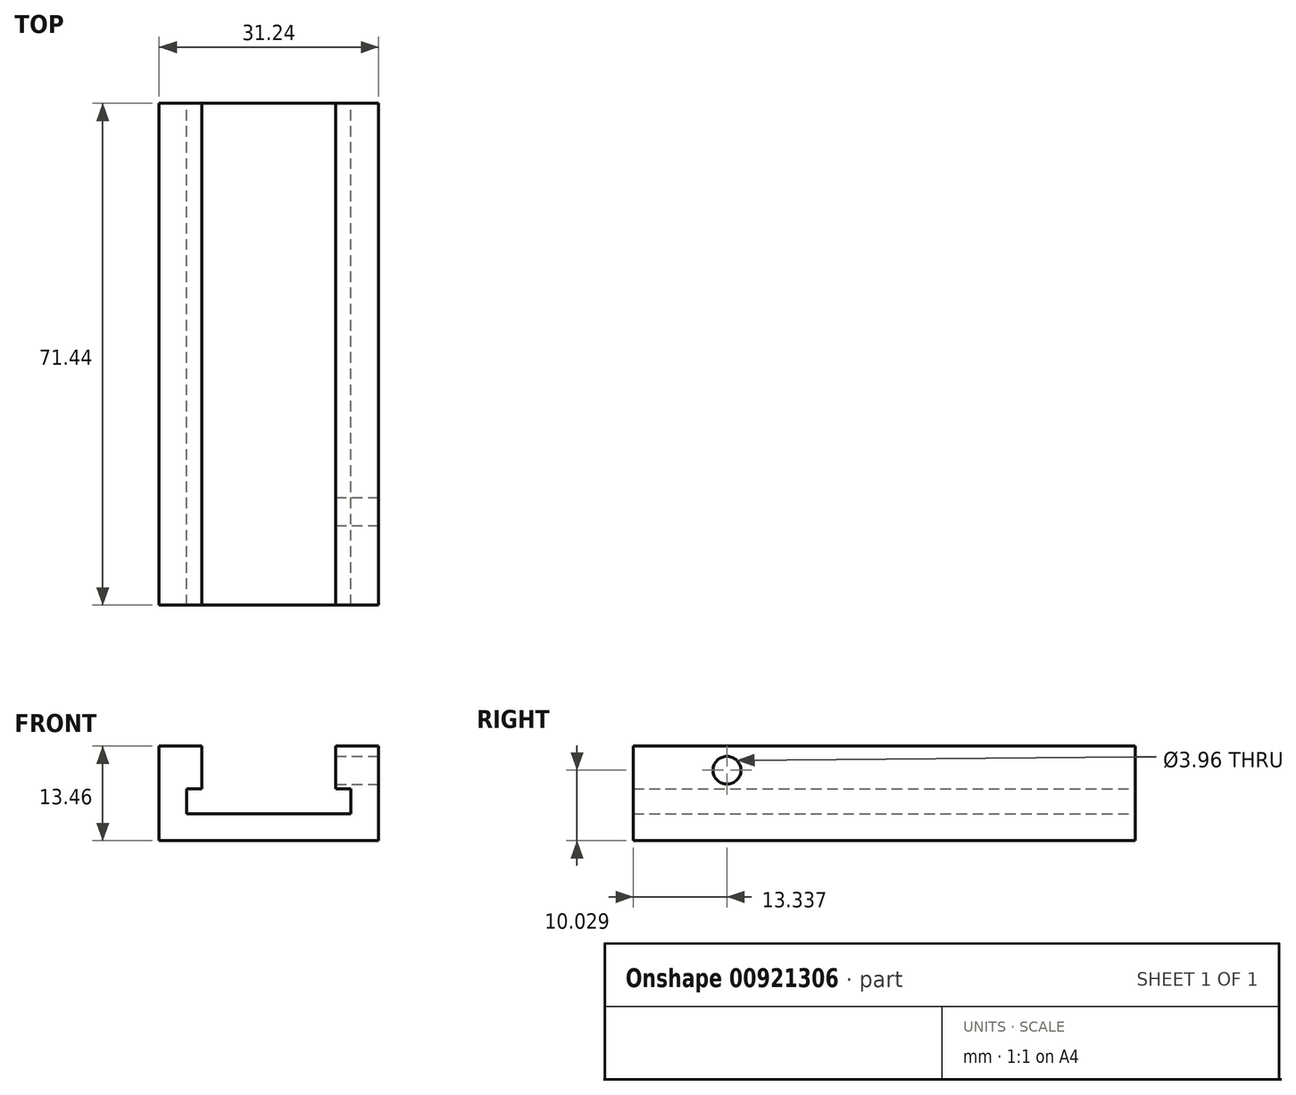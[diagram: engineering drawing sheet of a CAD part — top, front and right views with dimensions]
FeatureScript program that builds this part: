
annotation { "Feature Type Name" : "Feature", "Feature Type Description" : "" }
export const myFeature = defineFeature(function(context is Context, id is Id, definition is map)
    precondition{}
    {
        {
            var Q0;
            Q0=qCreatedBy(makeId("Front.planeOp"),FACE);
            var sketch = newSketch(context, id + "F0", { "sketchPlane" : qUnion([Q0])});
            skLineSegment(sketch, "E0", {"start": v(3.18, 12.19) * mm, "end": v(-2.91, 12.19) * mm});
            skLineSegment(sketch, "E1", {"start": v(-2.91, 12.19) * mm, "end": v(-2.91, -1.27) * mm});
            skLineSegment(sketch, "E2", {"start": v(-2.91, -1.27) * mm, "end": v(28.33, -1.27) * mm});
            skLineSegment(sketch, "E3", {"start": v(28.33, -1.27) * mm, "end": v(28.33, 12.19) * mm});
            skLineSegment(sketch, "E4", {"start": v(28.33, 12.19) * mm, "end": v(22.23, 12.19) * mm});
            skLineSegment(sketch, "E5", {"start": v(22.23, 12.19) * mm, "end": v(22.23, 6.1) * mm});
            skLineSegment(sketch, "E6", {"start": v(22.23, 6.1) * mm, "end": v(24.4, 6.1) * mm});
            skLineSegment(sketch, "E7", {"start": v(24.4, 6.1) * mm, "end": v(24.4, 2.54) * mm});
            skLineSegment(sketch, "E8", {"start": v(24.4, 2.54) * mm, "end": v(1.02, 2.54) * mm});
            skLineSegment(sketch, "E9", {"start": v(1.02, 2.54) * mm, "end": v(1.02, 6.1) * mm});
            skLineSegment(sketch, "E10", {"start": v(1.02, 6.1) * mm, "end": v(3.18, 6.1) * mm});
            skLineSegment(sketch, "E11", {"start": v(3.18, 6.1) * mm, "end": v(3.18, 12.19) * mm});
            skSolve(sketch);
        }
        {
            var Q0;
            Q0=makeQuery(id+"F0.imprint","IMPRINT",FACE,{"disambiguationData":[TD([[makeQuery(id+"F0.imprint","IMPRINT",EDGE,{"derivedFrom":sQuery(id+"F0.wireOp",EDGE,"E0")}),1.0]])]});
            extrude(context, id + "F1", {"entities" : qUnion([Q0]), "depth" : 71.44 * mm, "offsetDistance" : 25.4 * mm});
        }
        {
            var Q0;
            Q0=makeQuery(id+"F1.opExtrude","SWEPT_FACE",FACE,{"disambiguationData":[OSD([sQuery(id+"F0.wireOp",EDGE,"E3")])]});
            var sketch = newSketch(context, id + "F2", { "sketchPlane" : qUnion([Q0])});
            skCircle(sketch, "E12", {"center": v(-58.1, 8.76) * mm, "radius": 1.98 * mm});
            skSolve(sketch);
        }
        {
            var Q0;
            Q0=makeQuery(id+"F2.imprint","IMPRINT",FACE,{"disambiguationData":[TD([[makeQuery(id+"F2.imprint","IMPRINT",EDGE,{"derivedFrom":sQuery(id+"F2.wireOp",EDGE,"E12")}),1.0]])]});
            var Q1;
            Q1=sQuery(id+"F2.wireOp",EDGE,"E12");
            extrude(context, id + "F3", {"entities" : qUnion([Q0]), "operationType" : NewBodyOperationType.REMOVE, "surfaceEntities" : qUnion([Q1]), "endBound" : BoundingType.UP_TO_NEXT, "oppositeDirection" : true, "depth" : 25.4 * mm, "offsetDistance" : 25.4 * mm});
        }
    });
